# Revit family: ROSENBERG_SUPRABOX_COMFORT_V
name_source: partatom
category: Wyposażenie mechaniczne
revit_build: Autodesk Revit MEP 2016 (Build: 20150220_1215(x64)
units: mm (PartAtom-declared; Revit-internal decimal feet)

## family parameters
Numer OmniClass = 23.75.00.00
Oparty na płaszczyźnie roboczej = Nie
Punkt obliczania pomieszczeń = Nie
Tnij formami wycięć po wczytaniu = Nie
Typ części = Normalny
Tytuł OmniClass = Climate Control (HVAC)
Współdzielony = Nie
Wymiar okrągłego złącza = Użyj średnicy
Zawsze pionowo = Tak

## types (8) — shared parameters
Charakterystyka = https://rosenberg.pl
Częstotliwość pracy = 50 Hz
Karta katalogowa = https://rosenberg.pl
Maksymalna temp. powietrza przetłaczanego = 40 °C
Materiał = Rosenberg RAL
Napięcie znamionowe = 230 V
Obraz typu = <Brak>
Opis = Centrala kompaktowa SupraBox COMFORT
Producent = Rosenberg
URL = https://rosenberg.pl
Wykonanie = wewnętrzne, prawe
Średnica przyłącza odpł. kondensatu = 20 mm  [stored 0.0656168 ft]

## per-type parameters (varying)
- SupraBox Comfort 2000 V (WEW, PRAWE, REG): Ciśnienie dyspozycyjne=250.0 Pa; Dł.Centr=2220 mm; Dł.Przył1=58 mm  [stored 0.190289 ft]; Dł.Przył2=58 mm  [stored 0.190289 ft]; Filtr powietrza nawiew=F7: 538 x 608 x 96 mm; Filtr powietrza wywiew=M5: 538 x 608 x 96 mm; Klasa SFP=3; Masa=430.00 kg; Moc znamionowa=2 kW; Numer katalogowy=SBC200VGRIB0; Odsunięcie zawiasu=800 mm; Pobór mocy (wentylator 1)=1 kW; Pobór mocy (wentylator 2)=1 kW; Poz.B1=280 mm  [stored 0.918635 ft]; Poz.B2=510 mm  [stored 1.67323 ft]; Poz.Skr1=773 mm; Poz.Skr2=732 mm; Prąd znamionowy=12 A; Prędkość nominalna w króćcu=4.4 m/s; Regulacja=tak; Szer.Centr=770 mm; Szer.drzwi=1057 mm; Wydajność=2000.0 m³/h; Wys.Centr=1510 mm; Wys.T.=305 mm  [stored 1.00066 ft]; Wys.T2.=355 mm; para.pozB2=790 mm; para.sr.void=395 mm  [stored 1.29593 ft]; Średnica przyłącza P1=400 mm  [stored 1.31234 ft]
- SupraBox Comfort 1500 V (WEW, PRAWE, REG): Ciśnienie dyspozycyjne=200.0 Pa; Dł.Centr=1980 mm; Dł.Przył1=57 mm  [stored 0.187008 ft]; Dł.Przył2=57 mm  [stored 0.187008 ft]; Filtr powietrza nawiew=F7: 468 x 548 x 96 mm; Filtr powietrza wywiew=M5:468 x 548 x 96 mm; Klasa SFP=3; Masa=315.00 kg; Moc znamionowa=1 kW; Numer katalogowy=SBC150VGRIB0; Odsunięcie zawiasu=750 mm; Pobór mocy (wentylator 1)=0 kW; Pobór mocy (wentylator 2)=0 kW; Poz.B1=255 mm  [stored 0.836614 ft]; Poz.B2=450 mm  [stored 1.47638 ft]; Poz.Skr1=686 mm  [stored 2.25066 ft]; Poz.Skr2=651 mm; Prąd znamionowy=6 A; Prędkość nominalna w króćcu=4.2 m/s; Regulacja=tak; Szer.Centr=710 mm; Szer.drzwi=937 mm; Wydajność=1500.0 m³/h; Wys.Centr=1365 mm; Wys.T.=275 mm; Wys.T2.=325 mm  [stored 1.06627 ft]; para.pozB2=705 mm  [stored 2.31299 ft]; para.sr.void=350 mm  [stored 1.14829 ft]; Średnica przyłącza P1=355 mm
- SupraBox Comfort 1100 V (WEW, PRAWE, REG): Ciśnienie dyspozycyjne=200.0 Pa; Dł.Centr=1740 mm; Dł.Przył1=57 mm  [stored 0.187008 ft]; Dł.Przył2=57 mm  [stored 0.187008 ft]; Filtr powietrza nawiew=F7: 398 x 508 x 96 mm; Filtr powietrza wywiew=M5: 398 x 508 x 96 mm; Klasa SFP=2; Masa=253.00 kg; Moc znamionowa=1 kW; Numer katalogowy=SBC110VGRIB0; Odsunięcie zawiasu=660 mm; Pobór mocy (wentylator 1)=0 kW; Pobór mocy (wentylator 2)=0 kW; Poz.B1=230 mm  [stored 0.754593 ft]; Poz.B2=390 mm  [stored 1.27953 ft]; Poz.Skr1=596 mm  [stored 1.95538 ft]; Poz.Skr2=569 mm  [stored 1.8668 ft]; Prąd znamionowy=4 A; Prędkość nominalna w króćcu=4.4 m/s; Regulacja=tak; Szer.Centr=630 mm  [stored 2.06693 ft]; Szer.drzwi=817 mm; Wydajność=1100.0 m³/h; Wys.Centr=1225 mm; Wys.T.=235 mm  [stored 0.770997 ft]; Wys.T2.=285 mm  [stored 0.935039 ft]; para.pozB2=620 mm  [stored 2.03412 ft]; para.sr.void=310 mm  [stored 1.01706 ft]; Średnica przyłącza P1=315 mm  [stored 1.03346 ft]
- SupraBox Comfort 800 V (WEW, PRAWE, REG): Ciśnienie dyspozycyjne=150.0 Pa; Dł.Centr=1470 mm; Dł.Przył1=57 mm  [stored 0.187008 ft]; Dł.Przył2=57 mm  [stored 0.187008 ft]; Filtr powietrza nawiew=F7: 328 x 478 x 96 mm; Filtr powietrza wywiew=M5: 328 x 478 x 96 mm; Klasa SFP=2; Masa=209.00 kg; Moc znamionowa=0 kW; Numer katalogowy=SBC080VGRIB0; Odsunięcie zawiasu=630 mm  [stored 2.06693 ft]; Pobór mocy (wentylator 1)=0 kW; Pobór mocy (wentylator 2)=0 kW; Poz.B1=195 mm  [stored 0.639764 ft]; Poz.B2=325 mm  [stored 1.06627 ft]; Poz.Skr1=494 mm; Poz.Skr2=472 mm; Prąd znamionowy=6 A; Prędkość nominalna w króćcu=4.4 m/s; Regulacja=tak; Szer.Centr=600 mm; Szer.drzwi=682 mm; Wydajność=800.0 m³/h; Wys.Centr=1145 mm; Wys.T.=220 mm  [stored 0.721785 ft]; Wys.T2.=270 mm  [stored 0.885827 ft]; para.pozB2=520 mm  [stored 1.70604 ft]; para.sr.void=245 mm  [stored 0.803806 ft]; Średnica przyłącza P1=250 mm  [stored 0.82021 ft]
- SupraBox Comfort 2000 V (WEW, PRAWE): Ciśnienie dyspozycyjne=250.0 Pa; Dł.Centr=2220 mm; Dł.Przył1=57 mm  [stored 0.187008 ft]; Dł.Przył2=57 mm  [stored 0.187008 ft]; Filtr powietrza nawiew=F7: 538 x 608 x 96 mm; Filtr powietrza wywiew=M5: 538 x 608 x 96 mm; Klasa SFP=3; Masa=427.00 kg; Moc znamionowa=2 kW; Numer katalogowy=SBC200VGRIBE; Odsunięcie zawiasu=800 mm; Pobór mocy (wentylator 1)=1 kW; Pobór mocy (wentylator 2)=1 kW; Poz.B1=280 mm  [stored 0.918635 ft]; Poz.B2=510 mm  [stored 1.67323 ft]; Poz.Skr1=773 mm; Poz.Skr2=732 mm; Prąd znamionowy=12 A; Prędkość nominalna w króćcu=4.4 m/s; Regulacja=nie; Szer.Centr=770 mm; Szer.drzwi=1057 mm; Wydajność=2000.0 m³/h; Wys.Centr=1510 mm; Wys.T.=305 mm  [stored 1.00066 ft]; Wys.T2.=355 mm; para.pozB2=790 mm; para.sr.void=395 mm  [stored 1.29593 ft]; Średnica przyłącza P1=400 mm  [stored 1.31234 ft]
- SupraBox Comfort 1500 V (WEW, PRAWE): Ciśnienie dyspozycyjne=200.0 Pa; Dł.Centr=1980 mm; Dł.Przył1=57 mm  [stored 0.187008 ft]; Dł.Przył2=57 mm  [stored 0.187008 ft]; Filtr powietrza nawiew=F7: 468 x 548 x 96 mm; Filtr powietrza wywiew=M5: 468 x 548 x 96 mm; Klasa SFP=3; Masa=312.00 kg; Moc znamionowa=1 kW; Numer katalogowy=SBC150VGRIBE; Odsunięcie zawiasu=750 mm; Pobór mocy (wentylator 1)=0 kW; Pobór mocy (wentylator 2)=0 kW; Poz.B1=255 mm  [stored 0.836614 ft]; Poz.B2=450 mm  [stored 1.47638 ft]; Poz.Skr1=686 mm  [stored 2.25066 ft]; Poz.Skr2=651 mm; Prąd znamionowy=6 A; Prędkość nominalna w króćcu=4.2 m/s; Regulacja=nie; Szer.Centr=710 mm; Szer.drzwi=937 mm; Wydajność=1500.0 m³/h; Wys.Centr=1365 mm; Wys.T.=275 mm; Wys.T2.=325 mm  [stored 1.06627 ft]; para.pozB2=705 mm  [stored 2.31299 ft]; para.sr.void=350 mm  [stored 1.14829 ft]; Średnica przyłącza P1=355 mm
- SupraBox Comfort 1100 V (WEW, PRAWE): Ciśnienie dyspozycyjne=200.0 Pa; Dł.Centr=1740 mm; Dł.Przył1=57 mm  [stored 0.187008 ft]; Dł.Przył2=57 mm  [stored 0.187008 ft]; Filtr powietrza nawiew=F7: 398 x 508 x 96 mm; Filtr powietrza wywiew=M5: 398 x 508 x 96 mm; Klasa SFP=2; Masa=250.00 kg; Moc znamionowa=1 kW; Numer katalogowy=SBC110VGRIBE; Odsunięcie zawiasu=660 mm; Pobór mocy (wentylator 1)=0 kW; Pobór mocy (wentylator 2)=0 kW; Poz.B1=230 mm  [stored 0.754593 ft]; Poz.B2=390 mm  [stored 1.27953 ft]; Poz.Skr1=596 mm  [stored 1.95538 ft]; Poz.Skr2=569 mm  [stored 1.8668 ft]; Prąd znamionowy=6 A; Prędkość nominalna w króćcu=3.9 m/s; Regulacja=nie; Szer.Centr=630 mm  [stored 2.06693 ft]; Szer.drzwi=817 mm; Wydajność=1100.0 m³/h; Wys.Centr=1225 mm; Wys.T.=235 mm  [stored 0.770997 ft]; Wys.T2.=285 mm  [stored 0.935039 ft]; para.pozB2=620 mm  [stored 2.03412 ft]; para.sr.void=310 mm  [stored 1.01706 ft]; Średnica przyłącza P1=315 mm  [stored 1.03346 ft]
- SupraBox Comfort 800 V (WEW, PRAWE): Ciśnienie dyspozycyjne=150.0 Pa; Dł.Centr=1470 mm; Dł.Przył1=57 mm  [stored 0.187008 ft]; Dł.Przył2=58 mm  [stored 0.190289 ft]; Filtr powietrza nawiew=F7: 328 x 478 x 96 mm; Filtr powietrza wywiew=M5: 328 x 478 x 96 mm; Klasa SFP=2; Masa=206.00 kg; Moc znamionowa=0 kW; Numer katalogowy=SBC080VGRIBE; Odsunięcie zawiasu=630 mm  [stored 2.06693 ft]; Pobór mocy (wentylator 1)=0 kW; Pobór mocy (wentylator 2)=0 kW; Poz.B1=195 mm  [stored 0.639764 ft]; Poz.B2=325 mm  [stored 1.06627 ft]; Poz.Skr1=494 mm; Poz.Skr2=472 mm; Prąd znamionowy=6 A; Prędkość nominalna w króćcu=4.4 m/s; Regulacja=nie; Szer.Centr=600 mm; Szer.drzwi=682 mm; Wydajność=800.0 m³/h; Wys.Centr=1145 mm; Wys.T.=220 mm  [stored 0.721785 ft]; Wys.T2.=270 mm  [stored 0.885827 ft]; para.pozB2=520 mm  [stored 1.70604 ft]; para.sr.void=245 mm  [stored 0.803806 ft]; Średnica przyłącza P1=250 mm  [stored 0.82021 ft]

note: column(s) folded — value = type name in every type: Model

note: [stored X ft] marks values corroborated as IEEE doubles in the binary element streams (Revit-internal decimal feet)

## geometry (parser evidence)
native form markers: Blend x2, Sweep x25
no freeform markers — native parametric forms only
